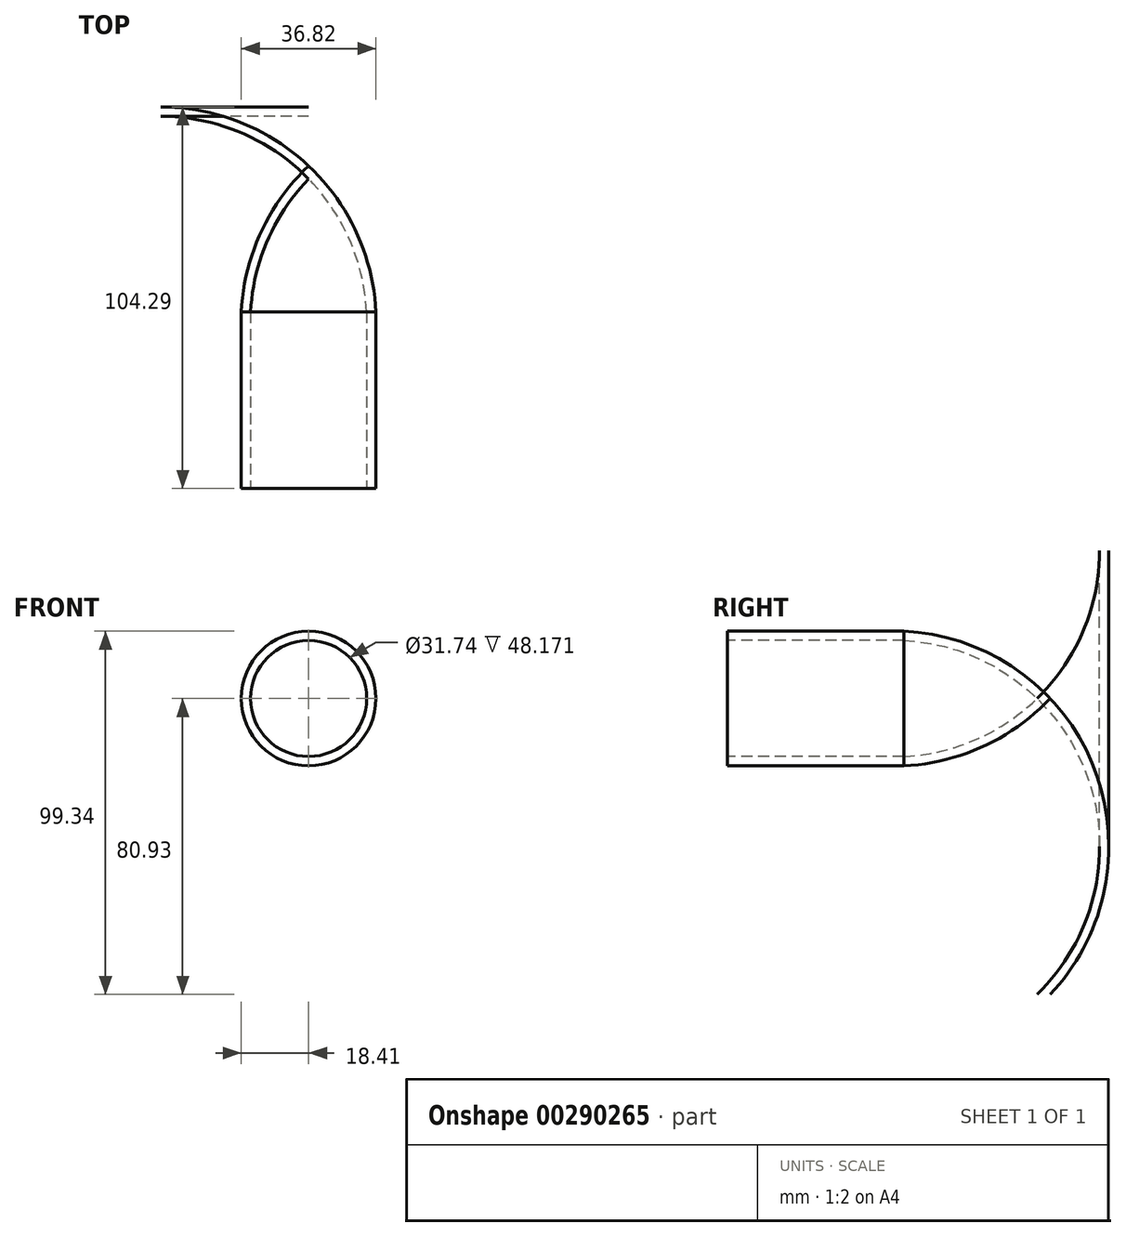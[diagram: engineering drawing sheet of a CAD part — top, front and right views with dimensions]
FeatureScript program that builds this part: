
annotation { "Feature Type Name" : "Feature", "Feature Type Description" : "" }
export const myFeature = defineFeature(function(context is Context, id is Id, definition is map)
    precondition{}
    {
        {
            var Q0;
            Q0=qCreatedBy(makeId("Top.planeOp"),FACE);
            var sketch = newSketch(context, id + "F0", { "sketchPlane" : qUnion([Q0])});
            skLineSegment(sketch, "E0", {"start": v(0, 0) * mm, "end": v(0, 88.2) * mm});
            skArc(sketch, "E1", {"start": v(0, 88.2) * mm, "mid": v(-13.07, 70) * mm, "end": v(-18.41, 48.23) * mm});
            skLineSegment(sketch, "E2", {"start": v(-18.41, 48.23) * mm, "end": v(-18.41, 0) * mm});
            skLineSegment(sketch, "E3", {"start": v(-18.41, 0) * mm, "end": v(0, 0) * mm});
            skSolve(sketch);
        }
        {
            var Q0;
            Q0=makeQuery(id+"F0.imprint","IMPRINT",FACE,{"disambiguationData":[TD([[makeQuery(id+"F0.imprint","IMPRINT",EDGE,{"derivedFrom":sQuery(id+"F0.wireOp",EDGE,"E0")}),1.0]])]});
            var Q1;
            Q1=sQuery(id+"F0.wireOp",EDGE,"E0");
            revolve(context, id + "F1", {"entities" : qUnion([Q0]), "axis" : qUnion([Q1]), "revolveType" : RevolveType.FULL});
        }
        {
            var Q0;
            Q0=makeQuery(id+"F1.opRevolve","SWEPT_FACE",FACE,{"disambiguationData":[OSD([sQuery(id+"F0.wireOp",EDGE,"E3")])]});
            shell(context, id + "F2", {"entities" : qUnion([Q0]), "thickness" : 2.54 * mm});
        }
    });
